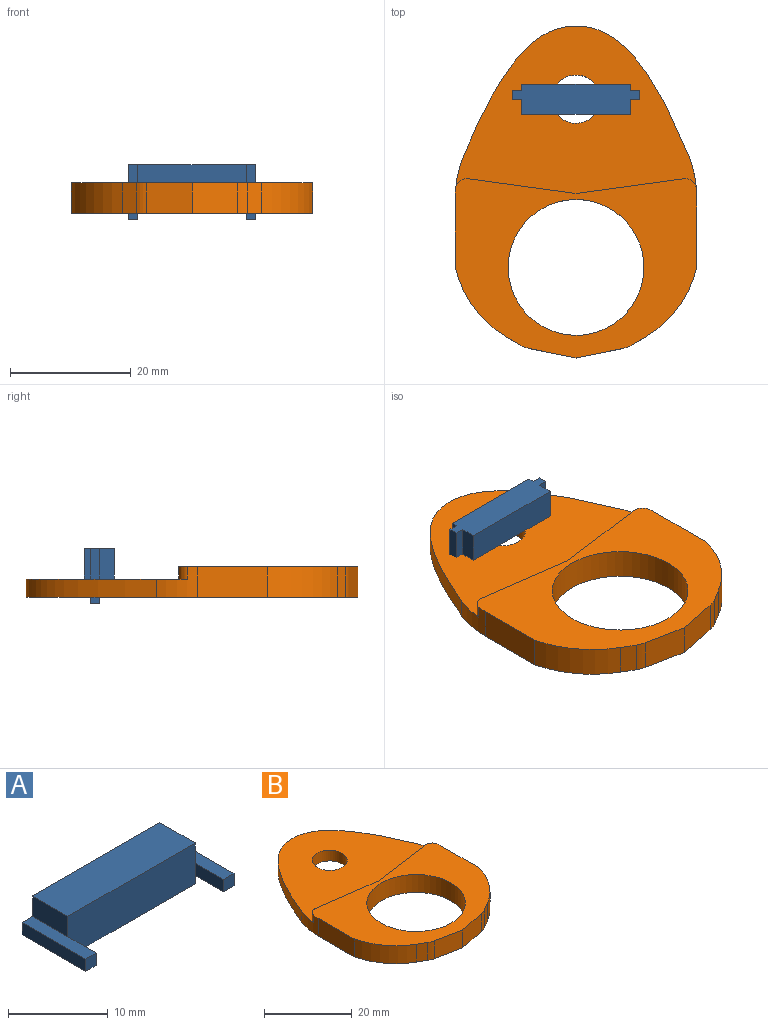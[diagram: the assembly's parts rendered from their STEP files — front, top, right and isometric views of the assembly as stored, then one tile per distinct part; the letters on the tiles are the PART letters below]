
ASSEMBLY  parts=2 mates=1
PART A: 18 faces, bbox 21x9x5 mm
  f0: plane 5x1mm, normal (-1,0,0), area 5mm2, adj f3,f5,f7,f15
  f1: plane 5x1mm, normal (1,0,0), area 5mm2, adj f3,f5,f7,f11
  f2: plane 5x2.5mm, normal (-1,0,0), area 12.5mm2, adj f3,f5,f6,f14
  f3: plane 18x5mm, normal (0,-1,0), area 90mm2, adj f0,f1,f2,f4,f6,f7,f8,f13
  f4: plane 5x2.5mm, normal (1,0,0), area 12.5mm2, adj f3,f5,f6,f9
  f5: plane 21x5mm, normal (0,1,0), area 94.5mm2, adj f0,f1,f2,f4,f6,f7,f9,f10
  f6: plane 18x5mm, normal (0,0,1), area 90mm2, adj f2,f3,f4,f5
  f7: plane 18x5mm, normal (0,0,-1), area 90mm2, adj f0,f1,f3,f5
  f8: plane 4x1.5mm, normal (-1,0,0), area 6mm2, adj f3,f9,f11,f12
  f9: plane 9x1.5mm, normal (0,0,1), area 13.5mm2, adj f4,f5,f8,f10,f12
  f10: plane 9x1.5mm, normal (1,0,0), area 13.5mm2, adj f5,f9,f11,f12
  f11: plane 9x1.5mm, normal (0,0,-1), area 13.5mm2, adj f1,f5,f8,f10,f12
  f12: plane 1.5x1.5mm, normal (0,-1,0), area 2.3mm2, adj f8,f9,f10,f11
  f13: plane 4x1.5mm, normal (1,0,0), area 6mm2, adj f3,f14,f15,f17
  f14: plane 9x1.5mm, normal (0,0,1), area 13.5mm2, adj f2,f5,f13,f16,f17
  f15: plane 9x1.5mm, normal (0,0,-1), area 13.5mm2, adj f0,f5,f13,f16,f17
  f16: plane 9x1.5mm, normal (-1,0,0), area 13.5mm2, adj f5,f14,f15,f17
  f17: plane 1.5x1.5mm, normal (0,-1,0), area 2.2mm2, adj f13,f14,f15,f16
PART B: 22 faces, bbox 40x56.4x5 mm
  f0: plane 40x29.71mm, normal (0,0,1), area 585.9mm2, adj f3,f4,f5,f6,f7,f8,f9,f12
  f1: extruded ~37.38x21.67mm, area 181.1mm2, adj f10,f11,f18,f19
  f2: cylinder r=4mm len=8mm, axis (0,0,-1), area 75.4mm2, adj f10,f11
  f3: plane 11.67x5mm, normal (1,0,0), area 58.4mm2, adj f0,f10,f15,f18
  f4: plane 11.56x5mm, normal (-1,0,0), area 57.8mm2, adj f0,f10,f14,f19
  f5: plane 5x2.34mm, normal (-0.5,-0.86,0), area 13.5mm2, adj f0,f10,f14,f20
  f6: plane 7.59x5mm, normal (-0.2,-0.98,0), area 38.7mm2, adj f0,f7,f10,f20
  f7: plane 7.59x5mm, normal (0.2,-0.98,0), area 38.7mm2, adj f0,f6,f10,f21
  f8: plane 5x2.34mm, normal (0.5,-0.86,0), area 13.5mm2, adj f0,f10,f15,f21
  f9: cylinder r=11.25mm len=22.5mm, axis (0,0,-1), area 353.4mm2, adj f0,f10
  f10: plane 56.41x40mm, normal (0,0,-1), area 1274.4mm2, adj f1,f2,f3,f4,f5,f6,f7,f8
  f11: plane 40x29.16mm, normal (0,0,1), area 688.5mm2, adj f1,f2,f12,f13,f16,f17,f18,f19
  f12: plane 17.73x2.44mm, normal (-0.14,0.99,0), area 35.8mm2, adj f0,f11,f13,f17
  f13: plane 17.73x2.44mm, normal (0.14,0.99,0), area 35.8mm2, adj f0,f11,f12,f16
  f14: cylinder r=18.14mm len=11.54mm, axis (0,0,-1), area 73.8mm2, adj f0,f4,f5,f10
  f15: cylinder r=18.13mm len=11.54mm, axis (0,0,-1), area 73.8mm2, adj f0,f3,f8,f10
  f16: cylinder r=2mm len=2.19mm, axis (0,0,1), area 5.7mm2, adj f0,f11,f13,f19
  f17: cylinder r=2mm len=2.21mm, axis (0,0,1), area 5.8mm2, adj f0,f11,f12,f18
  f18: cylinder r=18mm len=6.65mm, axis (0,0,-1), area 23.5mm2, adj f0,f1,f3,f10,f11,f17
  f19: cylinder r=18mm len=6.84mm, axis (0,0,-1), area 24.5mm2, adj f0,f1,f4,f10,f11,f16
  f20: cylinder r=5mm len=5mm, axis (0,0,-1), area 8.2mm2, adj f0,f5,f6,f10
  f21: cylinder r=5mm len=5mm, axis (0,0,-1), area 8.2mm2, adj f0,f7,f8,f10
PLACE A rot(axis=(1,0,0),90deg) t=(-5.1,20.82,4.92)mm
PLACE B t=(3.9,-9.56,1.92)mm
MATE fastened A.f3 <-> B.f2  axis (0,0,-1) through (3.9,18.32,4.92)mm
